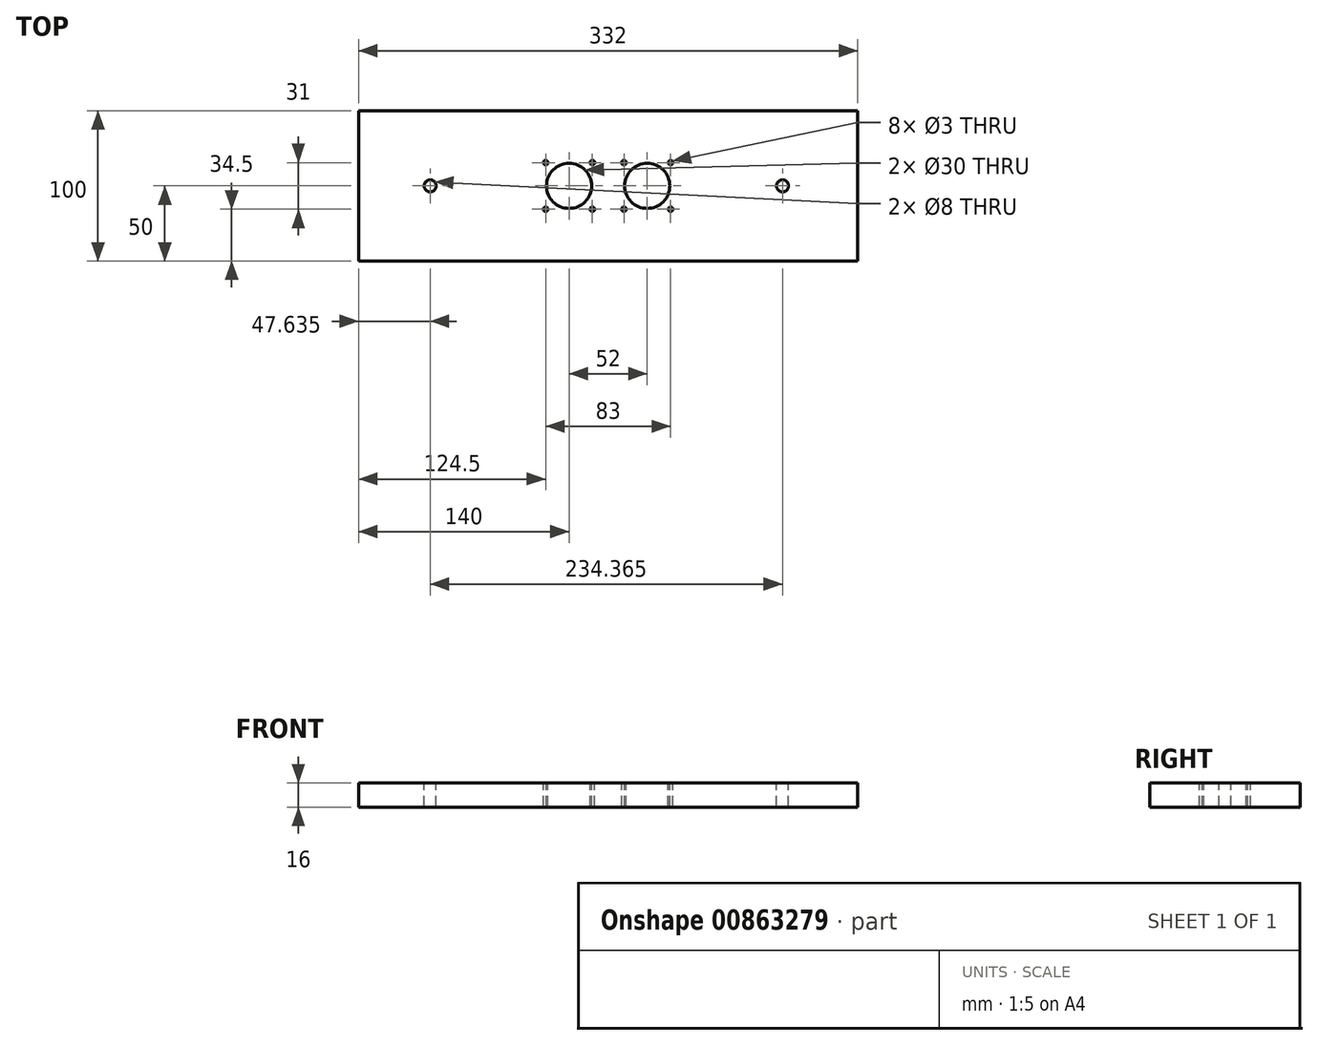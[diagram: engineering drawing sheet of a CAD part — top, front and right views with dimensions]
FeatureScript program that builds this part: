
annotation { "Feature Type Name" : "Feature", "Feature Type Description" : "" }
export const myFeature = defineFeature(function(context is Context, id is Id, definition is map)
    precondition{}
    {
        {
            var Q0;
            Q0=qCreatedBy(makeId("Top.planeOp"),FACE);
            var sketch = newSketch(context, id + "F0", { "sketchPlane" : qUnion([Q0])});
            skLineSegment(sketch, "E0.bottom", {"start": v(0, 0) * mm, "end": v(332, 0) * mm});
            skLineSegment(sketch, "E0.top", {"start": v(0, 100) * mm, "end": v(332, 100) * mm});
            skLineSegment(sketch, "E0.left", {"start": v(0, 0) * mm, "end": v(0, 100) * mm});
            skLineSegment(sketch, "E0.right", {"start": v(332, 0) * mm, "end": v(332, 100) * mm});
            skSolve(sketch);
        }
        {
            var Q0;
            Q0=makeQuery(id+"F0.imprint","IMPRINT",FACE,{"disambiguationData":[TD([[makeQuery(id+"F0.imprint","IMPRINT",EDGE,{"derivedFrom":sQuery(id+"F0.wireOp",EDGE,"E0.bottom")}),1.0]])]});
            extrude(context, id + "F1", {"entities" : qUnion([Q0]), "depth" : 16 * mm, "offsetDistance" : 25 * mm});
        }
        {
            var Q0;
            Q0=makeQuery(id+"F1.opExtrude","CAP_FACE",FACE,{"disambiguationData":[OSD([sQuery(id+"F0.wireOp",EDGE,"E0.bottom"),sQuery(id+"F0.wireOp",EDGE,"E0.top"),sQuery(id+"F0.wireOp",EDGE,"E0.left"),sQuery(id+"F0.wireOp",EDGE,"E0.right")])],"isStart":false});
            var sketch = newSketch(context, id + "F2", { "sketchPlane" : qUnion([Q0])});
            skLineSegment(sketch, "E1", {"start": v(0, 0) * mm, "end": v(140, 0) * mm});
            skLineSegment(sketch, "E2", {"start": v(332, 0) * mm, "end": v(192, 0) * mm});
            skLineSegment(sketch, "E3", {"start": v(140, 0) * mm, "end": v(140, 50) * mm});
            skLineSegment(sketch, "E4", {"start": v(192, 0) * mm, "end": v(192, 50) * mm});
            skCircle(sketch, "E5", {"center": v(140, 50) * mm, "radius": 15 * mm});
            skCircle(sketch, "E6", {"center": v(192, 50) * mm, "radius": 15 * mm});
            skLineSegment(sketch, "E7", {"start": v(140, 50) * mm, "end": v(155.5, 50) * mm});
            skLineSegment(sketch, "E8", {"start": v(155.5, 50) * mm, "end": v(155.5, 65.5) * mm});
            skCircle(sketch, "E9", {"center": v(155.5, 65.5) * mm, "radius": 1.5 * mm});
            skLineSegment(sketch, "E10", {"start": v(192, 50) * mm, "end": v(176.5, 50) * mm});
            skLineSegment(sketch, "E11", {"start": v(176.5, 50) * mm, "end": v(176.5, 65.5) * mm});
            skCircle(sketch, "E12", {"center": v(176.5, 65.5) * mm, "radius": 1.5 * mm});
            skLineSegment(sketch, "E13.bottom", {"start": v(155.5, 65.5) * mm, "end": v(124.5, 65.5) * mm});
            skLineSegment(sketch, "E13.top", {"start": v(155.5, 34.5) * mm, "end": v(124.5, 34.5) * mm});
            skLineSegment(sketch, "E13.left", {"start": v(155.5, 65.5) * mm, "end": v(155.5, 34.5) * mm});
            skLineSegment(sketch, "E13.right", {"start": v(124.5, 65.5) * mm, "end": v(124.5, 34.5) * mm});
            skLineSegment(sketch, "E14", {"start": v(140, 50) * mm, "end": v(124.5, 50) * mm});
            skCircle(sketch, "E15", {"center": v(124.5, 65.5) * mm, "radius": 1.5 * mm});
            skCircle(sketch, "E16", {"center": v(124.5, 34.5) * mm, "radius": 1.5 * mm});
            skCircle(sketch, "E17", {"center": v(155.5, 34.5) * mm, "radius": 1.5 * mm});
            skLineSegment(sketch, "E18.bottom", {"start": v(176.5, 65.5) * mm, "end": v(207.5, 65.5) * mm});
            skLineSegment(sketch, "E18.top", {"start": v(176.5, 34.5) * mm, "end": v(207.5, 34.5) * mm});
            skLineSegment(sketch, "E18.left", {"start": v(176.5, 65.5) * mm, "end": v(176.5, 34.5) * mm});
            skLineSegment(sketch, "E18.right", {"start": v(207.5, 65.5) * mm, "end": v(207.5, 34.5) * mm});
            skLineSegment(sketch, "E19", {"start": v(192, 50) * mm, "end": v(207.5, 50) * mm});
            skCircle(sketch, "E20", {"center": v(207.5, 65.5) * mm, "radius": 1.5 * mm});
            skCircle(sketch, "E21", {"center": v(207.5, 34.5) * mm, "radius": 1.5 * mm});
            skCircle(sketch, "E22", {"center": v(176.5, 34.5) * mm, "radius": 1.5 * mm});
            skSolve(sketch);
        }
        {
            var Q0;
            {var subQ0=sQuery(id+"F2.wireOp",EDGE,"E14");var subQ1=sQuery(id+"F2.wireOp",EDGE,"E5");var subQ2=makeQuery(id+"F2.imprint","INTERSECT",VERTEX,{"derivedFrom":[subQ1,subQ0]});Q0=makeQuery(id+"F2.imprint","IMPRINT",FACE,{"disambiguationData":[TD([[makeQuery(id+"F2.imprint","IMPRINT",EDGE,{"disambiguationData":[TD([[subQ2,1.0]])],"derivedFrom":subQ1}),1.0]])]});}
            var Q1;
            {var subQ1=sQuery(id+"F2.wireOp",EDGE,"E3");var subQ3=sQuery(id+"F2.wireOp",EDGE,"E5");var subQ4=makeQuery(id+"F2.imprint","INTERSECT",VERTEX,{"derivedFrom":[subQ1,subQ3]});Q1=makeQuery(id+"F2.imprint","IMPRINT",FACE,{"disambiguationData":[TD([[makeQuery(id+"F2.imprint","IMPRINT",EDGE,{"disambiguationData":[TD([[subQ4,-1.0]])],"derivedFrom":subQ3}),1.0]])]});}
            var Q2;
            {var subQ1=sQuery(id+"F2.wireOp",EDGE,"E3");var subQ3=sQuery(id+"F2.wireOp",EDGE,"E5");var subQ4=makeQuery(id+"F2.imprint","INTERSECT",VERTEX,{"derivedFrom":[subQ1,subQ3]});Q2=makeQuery(id+"F2.imprint","IMPRINT",FACE,{"disambiguationData":[TD([[makeQuery(id+"F2.imprint","IMPRINT",EDGE,{"disambiguationData":[TD([[subQ4,1.0]])],"derivedFrom":subQ3}),1.0]])]});}
            var Q3;
            {var subQ0=sQuery(id+"F2.wireOp",EDGE,"E13.right");var subQ1=sQuery(id+"F2.wireOp",EDGE,"E13.bottom");var subQ2=makeQuery(id+"F2.imprint","INTERSECT",VERTEX,{"derivedFrom":[subQ1,subQ0]});Q3=makeQuery(id+"F2.imprint","IMPRINT",FACE,{"disambiguationData":[TD([[makeQuery(id+"F2.imprint","IMPRINT",EDGE,{"disambiguationData":[TD([[subQ2,1.0]])],"derivedFrom":subQ1}),-1.0]])]});}
            var Q4;
            {var subQ0=sQuery(id+"F2.wireOp",EDGE,"E13.right");var subQ1=sQuery(id+"F2.wireOp",EDGE,"E13.bottom");var subQ2=makeQuery(id+"F2.imprint","INTERSECT",VERTEX,{"derivedFrom":[subQ1,subQ0]});Q4=makeQuery(id+"F2.imprint","IMPRINT",FACE,{"disambiguationData":[TD([[makeQuery(id+"F2.imprint","IMPRINT",EDGE,{"disambiguationData":[TD([[subQ2,1.0]])],"derivedFrom":subQ1}),1.0]])]});}
            var Q5;
            {var subQ0=sQuery(id+"F2.wireOp",EDGE,"E13.right");var subQ1=sQuery(id+"F2.wireOp",EDGE,"E13.top");var subQ2=makeQuery(id+"F2.imprint","INTERSECT",VERTEX,{"derivedFrom":[subQ1,subQ0]});Q5=makeQuery(id+"F2.imprint","IMPRINT",FACE,{"disambiguationData":[TD([[makeQuery(id+"F2.imprint","IMPRINT",EDGE,{"disambiguationData":[TD([[subQ2,1.0]])],"derivedFrom":subQ1}),1.0]])]});}
            var Q6;
            {var subQ0=sQuery(id+"F2.wireOp",EDGE,"E13.right");var subQ1=sQuery(id+"F2.wireOp",EDGE,"E13.top");var subQ2=makeQuery(id+"F2.imprint","INTERSECT",VERTEX,{"derivedFrom":[subQ1,subQ0]});Q6=makeQuery(id+"F2.imprint","IMPRINT",FACE,{"disambiguationData":[TD([[makeQuery(id+"F2.imprint","IMPRINT",EDGE,{"disambiguationData":[TD([[subQ2,1.0]])],"derivedFrom":subQ1}),-1.0]])]});}
            var Q7;
            {var subQ0=sQuery(id+"F2.wireOp",EDGE,"E13.left");var subQ1=sQuery(id+"F2.wireOp",EDGE,"E13.top");var subQ2=makeQuery(id+"F2.imprint","INTERSECT",VERTEX,{"derivedFrom":[subQ1,subQ0]});Q7=makeQuery(id+"F2.imprint","IMPRINT",FACE,{"disambiguationData":[TD([[makeQuery(id+"F2.imprint","IMPRINT",EDGE,{"disambiguationData":[TD([[subQ2,-1.0]])],"derivedFrom":subQ1}),1.0]])]});}
            var Q8;
            {var subQ0=sQuery(id+"F2.wireOp",EDGE,"E13.left");var subQ1=sQuery(id+"F2.wireOp",EDGE,"E13.top");var subQ2=makeQuery(id+"F2.imprint","INTERSECT",VERTEX,{"derivedFrom":[subQ1,subQ0]});Q8=makeQuery(id+"F2.imprint","IMPRINT",FACE,{"disambiguationData":[TD([[makeQuery(id+"F2.imprint","IMPRINT",EDGE,{"disambiguationData":[TD([[subQ2,-1.0]])],"derivedFrom":subQ1}),-1.0]])]});}
            var Q9;
            {var subQ0=sQuery(id+"F2.wireOp",EDGE,"E13.bottom");var subQ1=sQuery(id+"F2.wireOp",EDGE,"E9");var subQ2=makeQuery(id+"F2.imprint","INTERSECT",VERTEX,{"derivedFrom":[subQ1,subQ0]});Q9=makeQuery(id+"F2.imprint","IMPRINT",FACE,{"disambiguationData":[TD([[makeQuery(id+"F2.imprint","IMPRINT",EDGE,{"disambiguationData":[TD([[subQ2,1.0]])],"derivedFrom":subQ1}),1.0]])]});}
            var Q10;
            {var subQ0=sQuery(id+"F2.wireOp",EDGE,"E13.bottom");var subQ1=sQuery(id+"F2.wireOp",EDGE,"E9");var subQ2=makeQuery(id+"F2.imprint","INTERSECT",VERTEX,{"derivedFrom":[subQ1,subQ0]});Q10=makeQuery(id+"F2.imprint","IMPRINT",FACE,{"disambiguationData":[TD([[makeQuery(id+"F2.imprint","IMPRINT",EDGE,{"disambiguationData":[TD([[subQ2,-1.0]])],"derivedFrom":subQ1}),1.0]])]});}
            var Q11;
            {var subQ1=sQuery(id+"F2.wireOp",EDGE,"E4");var subQ3=sQuery(id+"F2.wireOp",EDGE,"E6");var subQ4=makeQuery(id+"F2.imprint","INTERSECT",VERTEX,{"derivedFrom":[subQ1,subQ3]});Q11=makeQuery(id+"F2.imprint","IMPRINT",FACE,{"disambiguationData":[TD([[makeQuery(id+"F2.imprint","IMPRINT",EDGE,{"disambiguationData":[TD([[subQ4,-1.0]])],"derivedFrom":subQ3}),1.0]])]});}
            var Q12;
            {var subQ0=sQuery(id+"F2.wireOp",EDGE,"E10");var subQ1=sQuery(id+"F2.wireOp",EDGE,"E6");var subQ2=makeQuery(id+"F2.imprint","INTERSECT",VERTEX,{"derivedFrom":[subQ1,subQ0]});Q12=makeQuery(id+"F2.imprint","IMPRINT",FACE,{"disambiguationData":[TD([[makeQuery(id+"F2.imprint","IMPRINT",EDGE,{"disambiguationData":[TD([[subQ2,1.0]])],"derivedFrom":subQ1}),1.0]])]});}
            var Q13;
            {var subQ1=sQuery(id+"F2.wireOp",EDGE,"E4");var subQ3=sQuery(id+"F2.wireOp",EDGE,"E6");var subQ4=makeQuery(id+"F2.imprint","INTERSECT",VERTEX,{"derivedFrom":[subQ1,subQ3]});Q13=makeQuery(id+"F2.imprint","IMPRINT",FACE,{"disambiguationData":[TD([[makeQuery(id+"F2.imprint","IMPRINT",EDGE,{"disambiguationData":[TD([[subQ4,1.0]])],"derivedFrom":subQ3}),1.0]])]});}
            var Q14;
            {var subQ0=sQuery(id+"F2.wireOp",EDGE,"E18.bottom");var subQ1=sQuery(id+"F2.wireOp",EDGE,"E12");var subQ2=makeQuery(id+"F2.imprint","INTERSECT",VERTEX,{"derivedFrom":[subQ1,subQ0]});Q14=makeQuery(id+"F2.imprint","IMPRINT",FACE,{"disambiguationData":[TD([[makeQuery(id+"F2.imprint","IMPRINT",EDGE,{"disambiguationData":[TD([[subQ2,-1.0]])],"derivedFrom":subQ1}),1.0]])]});}
            var Q15;
            {var subQ0=sQuery(id+"F2.wireOp",EDGE,"E18.bottom");var subQ1=sQuery(id+"F2.wireOp",EDGE,"E12");var subQ2=makeQuery(id+"F2.imprint","INTERSECT",VERTEX,{"derivedFrom":[subQ1,subQ0]});Q15=makeQuery(id+"F2.imprint","IMPRINT",FACE,{"disambiguationData":[TD([[makeQuery(id+"F2.imprint","IMPRINT",EDGE,{"disambiguationData":[TD([[subQ2,1.0]])],"derivedFrom":subQ1}),1.0]])]});}
            var Q16;
            {var subQ0=sQuery(id+"F2.wireOp",EDGE,"E18.left");var subQ1=sQuery(id+"F2.wireOp",EDGE,"E18.top");var subQ2=makeQuery(id+"F2.imprint","INTERSECT",VERTEX,{"derivedFrom":[subQ1,subQ0]});Q16=makeQuery(id+"F2.imprint","IMPRINT",FACE,{"disambiguationData":[TD([[makeQuery(id+"F2.imprint","IMPRINT",EDGE,{"disambiguationData":[TD([[subQ2,-1.0]])],"derivedFrom":subQ1}),-1.0]])]});}
            var Q17;
            {var subQ0=sQuery(id+"F2.wireOp",EDGE,"E18.left");var subQ1=sQuery(id+"F2.wireOp",EDGE,"E18.top");var subQ2=makeQuery(id+"F2.imprint","INTERSECT",VERTEX,{"derivedFrom":[subQ1,subQ0]});Q17=makeQuery(id+"F2.imprint","IMPRINT",FACE,{"disambiguationData":[TD([[makeQuery(id+"F2.imprint","IMPRINT",EDGE,{"disambiguationData":[TD([[subQ2,-1.0]])],"derivedFrom":subQ1}),1.0]])]});}
            var Q18;
            {var subQ0=sQuery(id+"F2.wireOp",EDGE,"E18.right");var subQ1=sQuery(id+"F2.wireOp",EDGE,"E18.top");var subQ2=makeQuery(id+"F2.imprint","INTERSECT",VERTEX,{"derivedFrom":[subQ1,subQ0]});Q18=makeQuery(id+"F2.imprint","IMPRINT",FACE,{"disambiguationData":[TD([[makeQuery(id+"F2.imprint","IMPRINT",EDGE,{"disambiguationData":[TD([[subQ2,1.0]])],"derivedFrom":subQ1}),1.0]])]});}
            var Q19;
            {var subQ0=sQuery(id+"F2.wireOp",EDGE,"E18.right");var subQ1=sQuery(id+"F2.wireOp",EDGE,"E18.top");var subQ2=makeQuery(id+"F2.imprint","INTERSECT",VERTEX,{"derivedFrom":[subQ1,subQ0]});Q19=makeQuery(id+"F2.imprint","IMPRINT",FACE,{"disambiguationData":[TD([[makeQuery(id+"F2.imprint","IMPRINT",EDGE,{"disambiguationData":[TD([[subQ2,1.0]])],"derivedFrom":subQ1}),-1.0]])]});}
            var Q20;
            {var subQ0=sQuery(id+"F2.wireOp",EDGE,"E18.right");var subQ1=sQuery(id+"F2.wireOp",EDGE,"E18.bottom");var subQ2=makeQuery(id+"F2.imprint","INTERSECT",VERTEX,{"derivedFrom":[subQ1,subQ0]});Q20=makeQuery(id+"F2.imprint","IMPRINT",FACE,{"disambiguationData":[TD([[makeQuery(id+"F2.imprint","IMPRINT",EDGE,{"disambiguationData":[TD([[subQ2,1.0]])],"derivedFrom":subQ1}),1.0]])]});}
            var Q21;
            {var subQ0=sQuery(id+"F2.wireOp",EDGE,"E18.right");var subQ1=sQuery(id+"F2.wireOp",EDGE,"E18.bottom");var subQ2=makeQuery(id+"F2.imprint","INTERSECT",VERTEX,{"derivedFrom":[subQ1,subQ0]});Q21=makeQuery(id+"F2.imprint","IMPRINT",FACE,{"disambiguationData":[TD([[makeQuery(id+"F2.imprint","IMPRINT",EDGE,{"disambiguationData":[TD([[subQ2,1.0]])],"derivedFrom":subQ1}),-1.0]])]});}
            extrude(context, id + "F3", {"entities" : qUnion([Q0, Q1, Q2, Q3, Q4, Q5, Q6, Q7, Q8, Q9, Q10, Q11, Q12, Q13, Q14, Q15, Q16, Q17, Q18, Q19, Q20, Q21]), "operationType" : NewBodyOperationType.REMOVE, "oppositeDirection" : true, "depth" : 25 * mm, "offsetDistance" : 25 * mm});
        }
        {
            var Q0;
            Q0=makeQuery(id+"F1.opExtrude","CAP_FACE",FACE,{"disambiguationData":[OSD([sQuery(id+"F0.wireOp",EDGE,"E0.bottom"),sQuery(id+"F0.wireOp",EDGE,"E0.top"),sQuery(id+"F0.wireOp",EDGE,"E0.left"),sQuery(id+"F0.wireOp",EDGE,"E0.right")])],"isStart":false});
            var sketch = newSketch(context, id + "F4", { "sketchPlane" : qUnion([Q0])});
            skLineSegment(sketch, "E23", {"start": v(-2.37, 0) * mm, "end": v(47.63, 0) * mm});
            skLineSegment(sketch, "E24", {"start": v(47.63, 0) * mm, "end": v(47.63, 50) * mm});
            skLineSegment(sketch, "E25", {"start": v(332, 0) * mm, "end": v(282, 0) * mm});
            skLineSegment(sketch, "E26", {"start": v(282, 0) * mm, "end": v(282, 50) * mm});
            skCircle(sketch, "E27", {"center": v(47.63, 50) * mm, "radius": 4 * mm});
            skCircle(sketch, "E28", {"center": v(282, 50) * mm, "radius": 4 * mm});
            skSolve(sketch);
        }
        {
            var Q0;
            Q0=makeQuery(id+"F4.imprint","IMPRINT",FACE,{"disambiguationData":[TD([[makeQuery(id+"F4.imprint","IMPRINT",EDGE,{"derivedFrom":sQuery(id+"F4.wireOp",EDGE,"E27")}),1.0]])]});
            var Q1;
            Q1=makeQuery(id+"F4.imprint","IMPRINT",FACE,{"disambiguationData":[TD([[makeQuery(id+"F4.imprint","IMPRINT",EDGE,{"derivedFrom":sQuery(id+"F4.wireOp",EDGE,"E28")}),1.0]])]});
            extrude(context, id + "F5", {"entities" : qUnion([Q0, Q1]), "operationType" : NewBodyOperationType.REMOVE, "oppositeDirection" : true, "depth" : 25 * mm, "offsetDistance" : 25 * mm});
        }
    });
